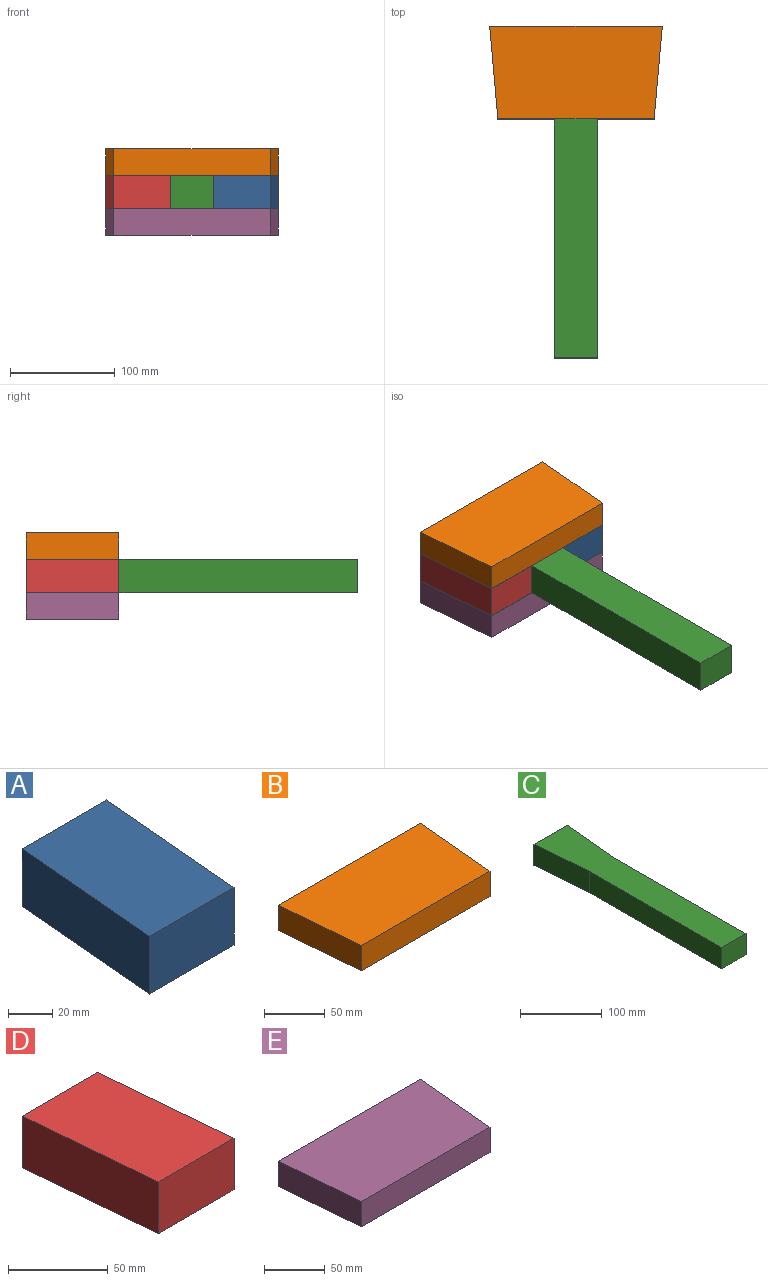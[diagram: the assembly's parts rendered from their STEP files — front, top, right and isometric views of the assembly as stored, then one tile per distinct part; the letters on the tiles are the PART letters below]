
ASSEMBLY  parts=5 mates=4
PART A: 6 faces, bbox 61.8x88.9x31.8 mm
  f0: plane 53.98x31.75mm, normal (0,1,0), area 1713.7mm2, adj f1,f3,f4,f5
  f1: plane 88.9x31.75mm, normal (-1,0.09,0), area 2833.4mm2, adj f0,f2,f4,f5
  f2: plane 53.98x31.75mm, normal (0,-1,0), area 1713.7mm2, adj f1,f3,f4,f5
  f3: plane 88.9x31.75mm, normal (1,-0.09,0), area 2833.4mm2, adj f0,f2,f4,f5
  f4: plane 88.9x61.75mm, normal (0,0,1), area 4798.4mm2, adj f0,f1,f2,f3
  f5: plane 88.9x61.75mm, normal (0,0,-1), area 4798.4mm2, adj f0,f1,f2,f3
PART B: 6 faces, bbox 165.1x88.9x25.4 mm
  f0: plane 165.1x88.9mm, normal (0,0,1), area 13985.9mm2, adj f1,f2,f3,f4
  f1: plane 88.9x25.4mm, normal (1,-0.09,0), area 2266.7mm2, adj f0,f3,f4,f5
  f2: plane 88.9x25.4mm, normal (-1,-0.09,0), area 2266.7mm2, adj f0,f3,f4,f5
  f3: plane 149.54x25.4mm, normal (0,-1,0), area 3798.4mm2, adj f0,f1,f2,f5
  f4: plane 165.1x25.4mm, normal (0,1,0), area 4193.5mm2, adj f0,f1,f2,f5
  f5: plane 165.1x88.9mm, normal (0,0,-1), area 13985.9mm2, adj f1,f2,f3,f4
PART C: 8 faces, bbox 57.2x317.5x31.8 mm
  f0: plane 41.59x31.75mm, normal (0,-1,0), area 1320.6mm2, adj f1,f5,f6,f7
  f1: plane 228.6x31.75mm, normal (1,0,0), area 7258mm2, adj f0,f2,f6,f7
  f2: plane 88.9x31.75mm, normal (1,-0.09,0), area 2833.4mm2, adj f1,f3,f6,f7
  f3: plane 57.15x31.75mm, normal (0,1,0), area 1814.5mm2, adj f2,f4,f6,f7
  f4: plane 88.9x31.75mm, normal (-1,-0.09,0), area 2833.4mm2, adj f3,f5,f6,f7
  f5: plane 228.6x31.75mm, normal (-1,0,0), area 7258.1mm2, adj f0,f4,f6,f7
  f6: plane 317.5x57.15mm, normal (0,0,-1), area 13897.7mm2, adj f0,f1,f2,f3,f4,f5
  f7: plane 317.5x57.15mm, normal (0,0,1), area 13897.7mm2, adj f0,f1,f2,f3,f4,f5
PART D: 6 faces, bbox 61.8x88.9x31.8 mm
  f0: plane 53.98x31.75mm, normal (0,1,0), area 1713.7mm2, adj f1,f3,f4,f5
  f1: plane 88.9x31.75mm, normal (-1,-0.09,0), area 2833.4mm2, adj f0,f2,f4,f5
  f2: plane 53.98x31.75mm, normal (0,-1,0), area 1713.7mm2, adj f1,f3,f4,f5
  f3: plane 88.9x31.75mm, normal (1,0.09,0), area 2833.4mm2, adj f0,f2,f4,f5
  f4: plane 88.9x61.75mm, normal (0,0,1), area 4798.4mm2, adj f0,f1,f2,f3
  f5: plane 88.9x61.75mm, normal (0,0,-1), area 4798.4mm2, adj f0,f1,f2,f3
PART E: 6 faces, bbox 165.1x88.9x25.4 mm
  f0: plane 165.1x25.4mm, normal (0,1,0), area 4193.5mm2, adj f2,f3,f4,f5
  f1: plane 149.54x25.4mm, normal (0,-1,0), area 3798.4mm2, adj f2,f3,f4,f5
  f2: plane 88.9x25.4mm, normal (1,-0.09,0), area 2266.7mm2, adj f0,f1,f4,f5
  f3: plane 88.9x25.4mm, normal (-1,-0.09,0), area 2266.7mm2, adj f0,f1,f4,f5
  f4: plane 165.1x88.9mm, normal (0,0,-1), area 13985.9mm2, adj f0,f1,f2,f3
  f5: plane 165.1x88.9mm, normal (0,0,1), area 13985.9mm2, adj f0,f1,f2,f3
PLACE A t=(-73.4,34.42,-72.14)mm
PLACE B t=(-73.4,34.42,-56.26)mm
PLACE C t=(-73.4,78.87,-56.26)mm
PLACE D t=(-73.4,34.42,-72.14)mm
PLACE E t=(-73.4,34.42,-56.26)mm
MATE fastened E.f5 <-> C.f6  axis (0,0,1) through (-73.4,78.87,-72.14)mm
MATE fastened A.f1 <-> C.f2  axis (-1,0.09,0) through (-48.71,34.42,-56.26)mm
MATE fastened B.f5 <-> C.f7  axis (0,0,-1) through (-73.4,78.87,-40.39)mm
MATE fastened D.f3 <-> C.f4  axis (1,0.09,0) through (-98.08,34.42,-56.26)mm
